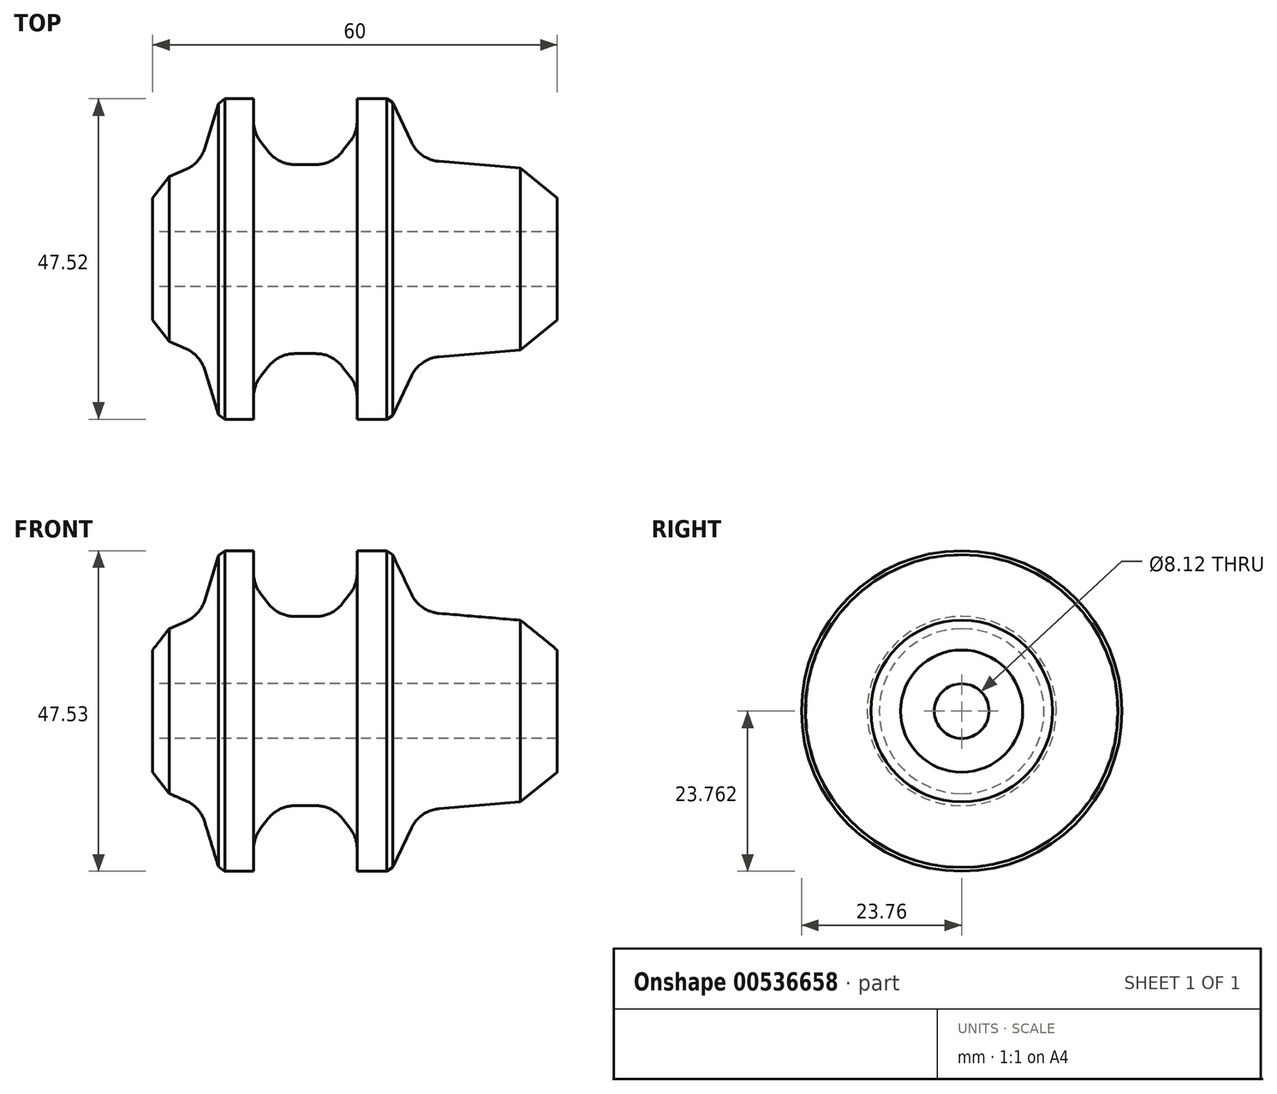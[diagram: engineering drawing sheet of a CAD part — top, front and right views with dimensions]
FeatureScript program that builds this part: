
annotation { "Feature Type Name" : "Feature", "Feature Type Description" : "" }
export const myFeature = defineFeature(function(context is Context, id is Id, definition is map)
    precondition{}
    {
        {
            var Q0;
            Q0=qCreatedBy(makeId("Front.planeOp"),FACE);
            var sketch = newSketch(context, id + "F0", { "sketchPlane" : qUnion([Q0])});
            skLineSegment(sketch, "E0.bottom", {"start": v(-30, -2.5) * mm, "end": v(30, -2.5) * mm});
            skLineSegment(sketch, "E0.left", {"start": v(-30, -2.5) * mm, "end": v(-30, 2.5) * mm});
            skLineSegment(sketch, "E0.right", {"start": v(30, -2.5) * mm, "end": v(30, 2.5) * mm});
            skPoint(sketch, "E0.middle", {"position": v(0, 0) * mm});
            skLineSegment(sketch, "E1", {"start": v(-20.03, 17.2) * mm, "end": v(-15.03, 17.2) * mm});
            skLineSegment(sketch, "E2", {"start": v(-15.03, 17.2) * mm, "end": v(-15.03, 12.2) * mm});
            skLineSegment(sketch, "E3", {"start": v(-15.03, 12.2) * mm, "end": v(-11.35, 7.47) * mm});
            skLineSegment(sketch, "E4", {"start": v(-11.35, 7.47) * mm, "end": v(-3.35, 7.47) * mm});
            skLineSegment(sketch, "E5", {"start": v(-3.35, 7.47) * mm, "end": v(0.33, 12.2) * mm});
            skLineSegment(sketch, "E6", {"start": v(0.33, 12.2) * mm, "end": v(0.33, 17.2) * mm});
            skLineSegment(sketch, "E7", {"start": v(0.33, 17.2) * mm, "end": v(5.33, 17.2) * mm});
            skLineSegment(sketch, "E8", {"start": v(5.33, 17.2) * mm, "end": v(9.62, 8.17) * mm});
            skLineSegment(sketch, "E9", {"start": v(9.62, 8.17) * mm, "end": v(24.57, 6.92) * mm});
            skLineSegment(sketch, "E10", {"start": v(24.57, 6.92) * mm, "end": v(30, 2.5) * mm});
            skPoint(sketch, "E11.end.orphan", {"position": v(6.03, 2.5) * mm});
            skLineSegment(sketch, "E12", {"start": v(-20.03, 17.2) * mm, "end": v(-22.96, 7.65) * mm});
            skLineSegment(sketch, "E13", {"start": v(-22.96, 7.65) * mm, "end": v(-27.56, 5.67) * mm});
            skLineSegment(sketch, "E14", {"start": v(-27.56, 5.67) * mm, "end": v(-30, 2.5) * mm});
            skLineSegment(sketch, "E15", {"start": v(-35.06, -6.56) * mm, "end": v(36.06, -6.56) * mm, "construction": true});
            skSolve(sketch);
        }
        {
            var Q0;
            Q0=makeQuery(id+"F0.imprint","IMPRINT",FACE,{"disambiguationData":[TD([[makeQuery(id+"F0.imprint","IMPRINT",EDGE,{"derivedFrom":sQuery(id+"F0.wireOp",EDGE,"E0.bottom")}),1.0]])]});
            var Q1;
            Q1=sQuery(id+"F0.wireOp",EDGE,"E15");
            revolve(context, id + "F1", {"entities" : qUnion([Q0]), "axis" : qUnion([Q1]), "revolveType" : RevolveType.FULL});
        }
        {
            var Q0;
            Q0=makeQuery(id+"F1.opRevolve","SWEPT_EDGE",EDGE,{"disambiguationData":[OSD([sQuery(id+"F0.wireOp",EDGE,"E3"),sQuery(id+"F0.wireOp",EDGE,"E4")])]});
            var Q1;
            Q1=makeQuery(id+"F1.opRevolve","SWEPT_EDGE",EDGE,{"disambiguationData":[OSD([sQuery(id+"F0.wireOp",EDGE,"E4"),sQuery(id+"F0.wireOp",EDGE,"E5")])]});
            var Q2;
            Q2=makeQuery(id+"F1.opRevolve","SWEPT_EDGE",EDGE,{"disambiguationData":[OSD([sQuery(id+"F0.wireOp",EDGE,"E5"),sQuery(id+"F0.wireOp",EDGE,"E6")])]});
            var Q3;
            Q3=makeQuery(id+"F1.opRevolve","SWEPT_EDGE",EDGE,{"disambiguationData":[OSD([sQuery(id+"F0.wireOp",EDGE,"E2"),sQuery(id+"F0.wireOp",EDGE,"E3")])]});
            var Q4;
            Q4=makeQuery(id+"F1.opRevolve","SWEPT_EDGE",EDGE,{"disambiguationData":[OSD([sQuery(id+"F0.wireOp",EDGE,"E8"),sQuery(id+"F0.wireOp",EDGE,"E9")])]});
            var Q5;
            Q5=makeQuery(id+"F1.opRevolve","SWEPT_EDGE",EDGE,{"disambiguationData":[OSD([sQuery(id+"F0.wireOp",EDGE,"E12"),sQuery(id+"F0.wireOp",EDGE,"E13")])]});
            fillet(context, id + "F2", {"entities" : qUnion([Q0, Q1, Q2, Q3, Q4, Q5]), "radius" : 5 * mm, "tangentPropagation" : true, "allowEdgeOverflow" : false});
        }
        {
            var Q0;
            Q0=makeQuery(id+"F1.opRevolve","SWEPT_EDGE",EDGE,{"disambiguationData":[OSD([sQuery(id+"F0.wireOp",EDGE,"E1"),sQuery(id+"F0.wireOp",EDGE,"E12")])]});
            var Q1;
            Q1=makeQuery(id+"F1.opRevolve","SWEPT_EDGE",EDGE,{"disambiguationData":[OSD([sQuery(id+"F0.wireOp",EDGE,"E7"),sQuery(id+"F0.wireOp",EDGE,"E8")])]});
            chamfer(context, id + "F3", {"entities" : qUnion([Q0, Q1]), "width" : 1 * mm, "tangentPropagation" : true});
        }
    });
